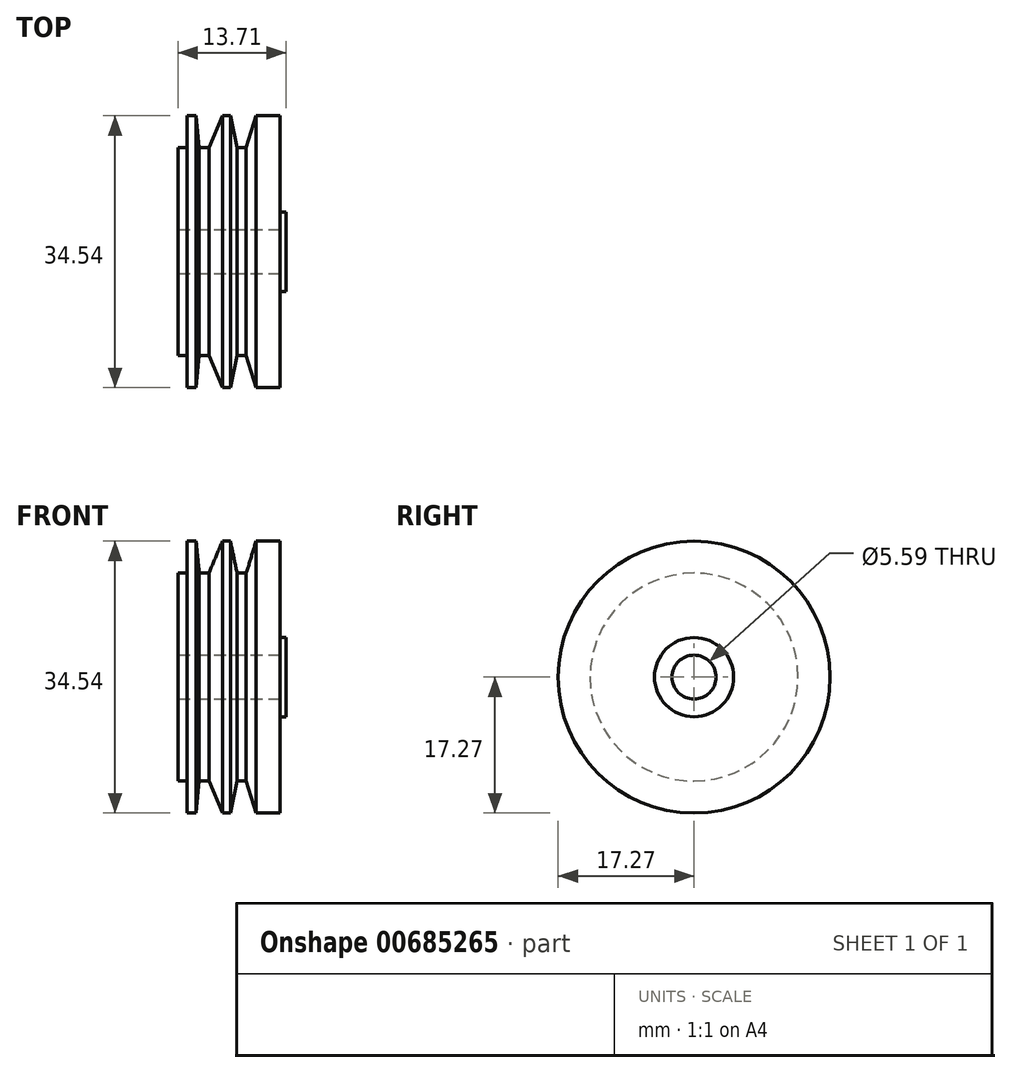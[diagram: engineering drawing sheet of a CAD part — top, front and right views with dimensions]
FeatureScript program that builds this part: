
annotation { "Feature Type Name" : "Feature", "Feature Type Description" : "" }
export const myFeature = defineFeature(function(context is Context, id is Id, definition is map)
    precondition{}
    {
        {
            var Q0;
            Q0=qCreatedBy(makeId("Front.planeOp"),FACE);
            var sketch = newSketch(context, id + "F0", { "sketchPlane" : qUnion([Q0])});
            skLineSegment(sketch, "E0", {"start": v(-9.15, 0) * mm, "end": v(-9.15, 13.2) * mm});
            skLineSegment(sketch, "E1", {"start": v(-9.15, 13.2) * mm, "end": v(-8, 13.2) * mm});
            skLineSegment(sketch, "E2", {"start": v(-8, 13.2) * mm, "end": v(-8, 17.27) * mm});
            skLineSegment(sketch, "E3", {"start": v(-8, 17.27) * mm, "end": v(-6.87, 17.27) * mm});
            skLineSegment(sketch, "E4", {"start": v(-6.87, 17.27) * mm, "end": v(-6.47, 13.2) * mm});
            skLineSegment(sketch, "E5", {"start": v(-6.47, 13.2) * mm, "end": v(-5.25, 13.2) * mm});
            skLineSegment(sketch, "E6", {"start": v(-5.25, 13.2) * mm, "end": v(-3.52, 17.27) * mm});
            skLineSegment(sketch, "E7", {"start": v(-3.52, 17.27) * mm, "end": v(-2.5, 17.27) * mm});
            skLineSegment(sketch, "E8", {"start": v(-2.5, 17.27) * mm, "end": v(-1.65, 13.2) * mm});
            skLineSegment(sketch, "E9", {"start": v(-1.65, 13.2) * mm, "end": v(-0.49, 13.2) * mm});
            skLineSegment(sketch, "E10", {"start": v(-0.49, 13.2) * mm, "end": v(0.75, 17.27) * mm});
            skLineSegment(sketch, "E11", {"start": v(0.75, 17.27) * mm, "end": v(3.8, 17.27) * mm});
            skLineSegment(sketch, "E12", {"start": v(3.8, 17.27) * mm, "end": v(3.8, 5.03) * mm});
            skLineSegment(sketch, "E13", {"start": v(3.8, 5.03) * mm, "end": v(4.56, 5.03) * mm});
            skLineSegment(sketch, "E14", {"start": v(4.56, 5.03) * mm, "end": v(4.56, 0) * mm});
            skPoint(sketch, "E15.end.orphan", {"position": v(3.8, 0) * mm});
            skLineSegment(sketch, "E16", {"start": v(-9.15, 0) * mm, "end": v(4.56, 0) * mm});
            skSolve(sketch);
        }
        {
            var Q0;
            Q0=makeQuery(id+"F0.imprint","IMPRINT",FACE,{"disambiguationData":[TD([[makeQuery(id+"F0.imprint","IMPRINT",EDGE,{"derivedFrom":sQuery(id+"F0.wireOp",EDGE,"E0")}),-1.0]])]});
            var Q1;
            Q1=sQuery(id+"F0.wireOp",EDGE,"E16");
            revolve(context, id + "F1", {"entities" : qUnion([Q0]), "axis" : qUnion([Q1]), "revolveType" : RevolveType.FULL});
        }
        {
            var Q0;
            Q0=makeQuery(id+"F1.opRevolve","SWEPT_FACE",FACE,{"disambiguationData":[OSD([sQuery(id+"F0.wireOp",EDGE,"E14")])]});
            var sketch = newSketch(context, id + "F2", { "sketchPlane" : qUnion([Q0])});
            skCircle(sketch, "E17", {"center": v(0, 0) * mm, "radius": 13.97 * mm});
            skCircle(sketch, "E18", {"center": v(0, 0) * mm, "radius": 2.8 * mm});
            skCircle(sketch, "E19", {"center": v(0, 0) * mm, "radius": 1.3 * mm});
            skPoint(sketch, "E20.start.orphan", {"position": v(-2.2, 4.52) * mm});
            skPoint(sketch, "E21.start.orphan", {"position": v(-2.2, -4.52) * mm});
            skLineSegment(sketch, "E22", {"start": v(1.27, -10.18) * mm, "end": v(1.27, -4.86) * mm});
            skLineSegment(sketch, "E23", {"start": v(-1.27, -10.18) * mm, "end": v(-1.27, -4.86) * mm});
            skLineSegment(sketch, "E24", {"start": v(-1.27, -10.18) * mm, "end": v(-1.27, -13.91) * mm});
            skLineSegment(sketch, "E25", {"start": v(1.27, -10.18) * mm, "end": v(1.27, -13.91) * mm});
            skLineSegment(sketch, "E26", {"start": v(8.48, -1.25) * mm, "end": v(8.48, -1.27) * mm});
            skLineSegment(sketch, "E27", {"start": v(8.48, 1.27) * mm, "end": v(4.86, 1.27) * mm});
            skLineSegment(sketch, "E28", {"start": v(4.86, 1.27) * mm, "end": v(13.91, 1.27) * mm});
            skLineSegment(sketch, "E29", {"start": v(-13.91, 1.27) * mm, "end": v(-4.86, 1.27) * mm});
            skLineSegment(sketch, "E30", {"start": v(-4.86, -1.27) * mm, "end": v(-13.91, -1.27) * mm});
            skLineSegment(sketch, "E31", {"start": v(-1.27, 4.86) * mm, "end": v(-1.27, 13.91) * mm});
            skLineSegment(sketch, "E32", {"start": v(1.27, 4.86) * mm, "end": v(1.27, 13.91) * mm});
            skPoint(sketch, "E33.end.orphan", {"position": v(-1.27, 9.5) * mm});
            skPoint(sketch, "E34.end.orphan", {"position": v(1.27, 9.5) * mm});
            skPoint(sketch, "E34.start.orphan", {"position": v(0, 9.5) * mm});
            skLineSegment(sketch, "E35", {"start": v(4.86, -1.27) * mm, "end": v(13.92, -1.23) * mm});
            skPoint(sketch, "E36.end.orphan", {"position": v(-10.29, -1.27) * mm});
            skPoint(sketch, "E37.orphan", {"position": v(-5.03, 0) * mm});
            skPoint(sketch, "E38.start.orphan", {"position": v(5.03, 0) * mm});
            skPoint(sketch, "E39.orphan", {"position": v(0, 13.97) * mm});
            skPoint(sketch, "E40.start.orphan", {"position": v(0, 5.03) * mm});
            skPoint(sketch, "E41.start.orphan", {"position": v(0, -5.03) * mm});
            skPoint(sketch, "E42.end.orphan", {"position": v(-10.29, 1.27) * mm});
            skSolve(sketch);
        }
        {
            var Q0;
            Q0=sQuery(id+"F2.wireOp",VERTEX,"E17.center");
            var Q1;
            Q1=makeQuery(id+"F1.opRevolve","SWEPT_BODY",BODY,{"disambiguationData":[OSD([sQuery(id+"F0.wireOp",EDGE,"E0"),sQuery(id+"F0.wireOp",EDGE,"E1"),sQuery(id+"F0.wireOp",EDGE,"E2"),sQuery(id+"F0.wireOp",EDGE,"E3"),sQuery(id+"F0.wireOp",EDGE,"E4"),sQuery(id+"F0.wireOp",EDGE,"E5"),sQuery(id+"F0.wireOp",EDGE,"E6"),sQuery(id+"F0.wireOp",EDGE,"E7"),sQuery(id+"F0.wireOp",EDGE,"E8"),sQuery(id+"F0.wireOp",EDGE,"E9"),sQuery(id+"F0.wireOp",EDGE,"E10"),sQuery(id+"F0.wireOp",EDGE,"E11"),sQuery(id+"F0.wireOp",EDGE,"E12"),sQuery(id+"F0.wireOp",EDGE,"E13"),sQuery(id+"F0.wireOp",EDGE,"E14"),sQuery(id+"F0.wireOp",EDGE,"E16")])]});
            hole(context, id + "F3", {"style" : HoleStyle.SIMPLE, "endStyle" : HoleEndStyle.THROUGH, "holeDiameter" : 5.6 * mm, "majorDiameter" : 6.35 * mm, "isTappedThrough" : true, "tappedDepth" : 12.7 * mm, "tapClearance" : 3, "locations" : qUnion([Q0]), "scope" : qUnion([Q1])});
        }
    });
